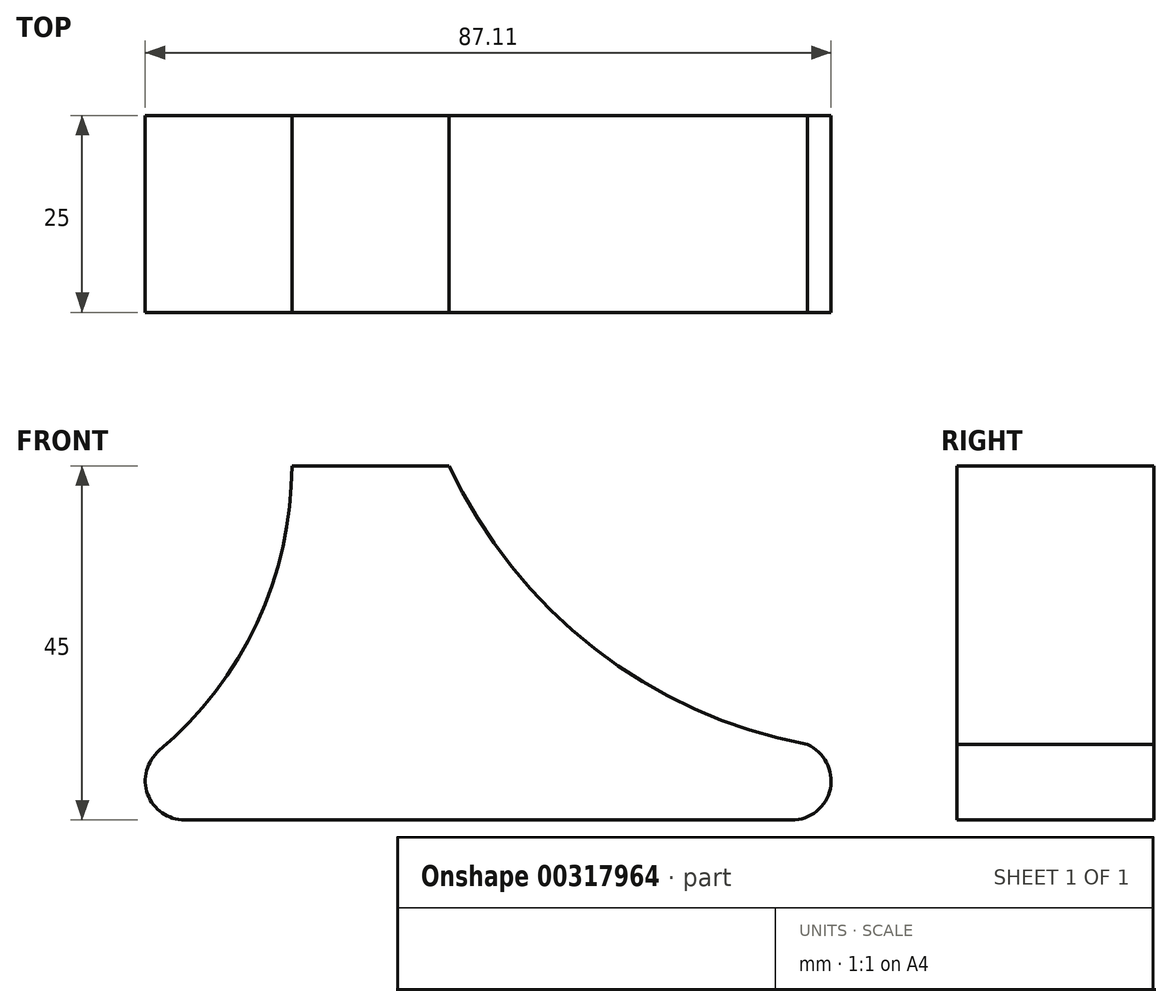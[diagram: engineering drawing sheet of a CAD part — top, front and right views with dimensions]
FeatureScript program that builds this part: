
annotation { "Feature Type Name" : "Feature", "Feature Type Description" : "" }
export const myFeature = defineFeature(function(context is Context, id is Id, definition is map)
    precondition{}
    {
        {
            var Q0;
            Q0=qCreatedBy(makeId("Front.planeOp"),FACE);
            var sketch = newSketch(context, id + "F0", { "sketchPlane" : qUnion([Q0])});
            skLineSegment(sketch, "E0.bottom", {"start": v(0, 0) * mm, "end": v(20, 0) * mm});
            skLineSegment(sketch, "E0.top", {"start": v(0, -45) * mm, "end": v(20, -45) * mm});
            skLineSegment(sketch, "E0.left", {"start": v(0, 0) * mm, "end": v(0, -45) * mm});
            skLineSegment(sketch, "E0.right", {"start": v(20, 0) * mm, "end": v(20, -45) * mm});
            skLineSegment(sketch, "E1", {"start": v(0, -45) * mm, "end": v(-13.61, -45) * mm});
            skArc(sketch, "E2", {"start": v(-16.83, -36.18) * mm, "mid": v(-4.41, -19.95) * mm, "end": v(0, 0) * mm});
            skPoint(sketch, "E3.visualSharp", {"position": v(-32.76, -45) * mm});
            skArc(sketch, "E3.filletArc", {"start": v(-16.83, -36.18) * mm, "mid": v(-18.3, -41.71) * mm, "end": v(-13.61, -45) * mm});
            skLineSegment(sketch, "E4", {"start": v(20, -45) * mm, "end": v(63.5, -45) * mm});
            skPoint(sketch, "E5.visualSharp", {"position": v(111.62, -45) * mm});
            skArc(sketch, "E5.filletArc", {"start": v(63.5, -45) * mm, "mid": v(68.4, -41.02) * mm, "end": v(65.5, -35.41) * mm});
            skArc(sketch, "E6", {"start": v(20, 0) * mm, "mid": v(38.47, -23.2) * mm, "end": v(65.5, -35.41) * mm});
            skSolve(sketch);
        }
        {
            var Q0;
            Q0=makeQuery(id+"F0.imprint","IMPRINT",FACE,{"disambiguationData":[TD([[makeQuery(id+"F0.imprint","IMPRINT",EDGE,{"derivedFrom":sQuery(id+"F0.wireOp",EDGE,"E0.left")}),-1.0]])]});
            var Q1;
            Q1=makeQuery(id+"F0.imprint","IMPRINT",FACE,{"disambiguationData":[TD([[makeQuery(id+"F0.imprint","IMPRINT",EDGE,{"derivedFrom":sQuery(id+"F0.wireOp",EDGE,"E0.bottom")}),-1.0]])]});
            var Q2;
            Q2=makeQuery(id+"F0.imprint","IMPRINT",FACE,{"disambiguationData":[TD([[makeQuery(id+"F0.imprint","IMPRINT",EDGE,{"derivedFrom":sQuery(id+"F0.wireOp",EDGE,"E0.right")}),1.0]])]});
            extrude(context, id + "F1", {"entities" : qUnion([Q0, Q1, Q2]), "depth" : 25 * mm});
        }
    });
